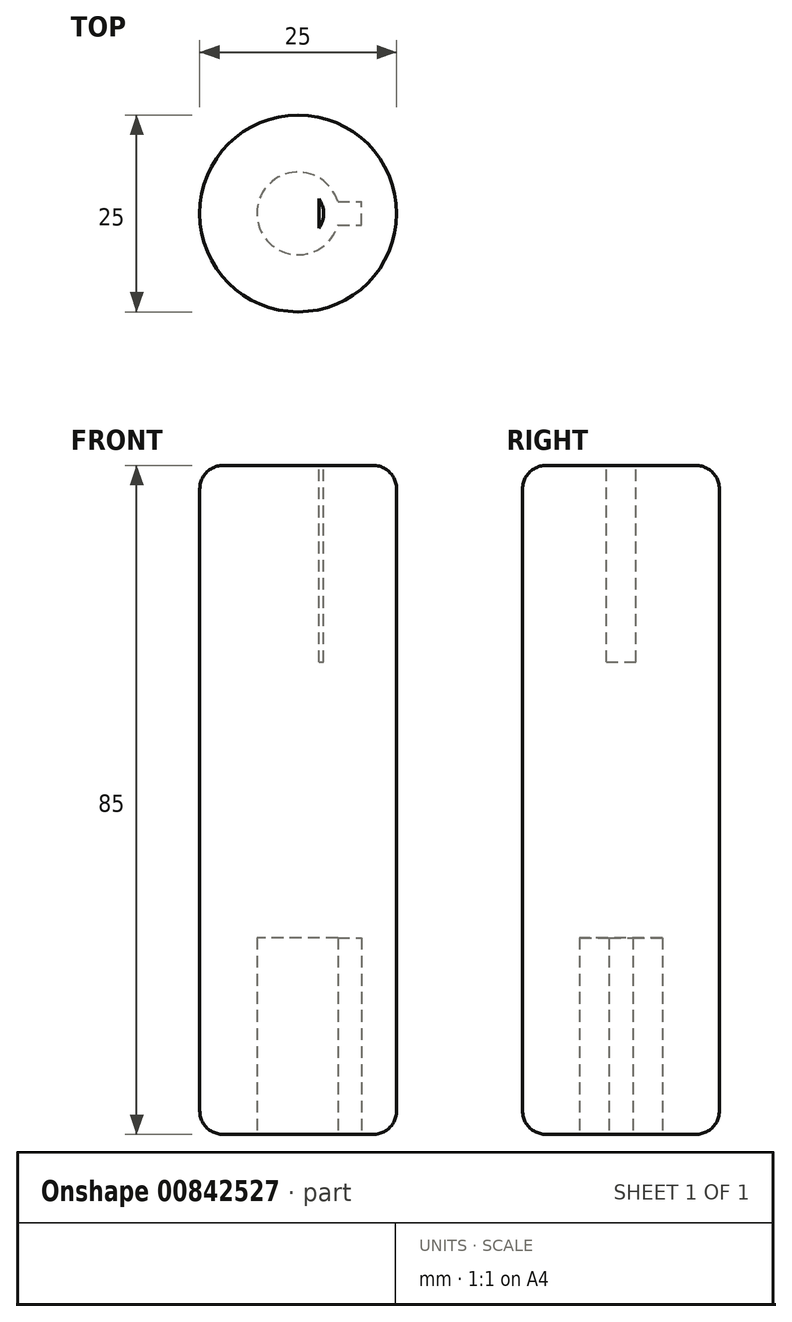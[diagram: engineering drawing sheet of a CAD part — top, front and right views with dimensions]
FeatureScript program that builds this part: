
annotation { "Feature Type Name" : "Feature", "Feature Type Description" : "" }
export const myFeature = defineFeature(function(context is Context, id is Id, definition is map)
    precondition{}
    {
        {
            var Q0;
            Q0=qCreatedBy(makeId("Top.planeOp"),FACE);
            var sketch = newSketch(context, id + "F0", { "sketchPlane" : qUnion([Q0])});
            skCircle(sketch, "E0", {"center": v(0, 0) * mm, "radius": 5.25 * mm});
            skCircle(sketch, "E1", {"center": v(0, 0) * mm, "radius": 12.5 * mm});
            skLineSegment(sketch, "E2.bottom", {"start": v(5.03, -1.5) * mm, "end": v(8.03, -1.5) * mm});
            skLineSegment(sketch, "E2.top", {"start": v(5.03, 1.5) * mm, "end": v(8.03, 1.5) * mm});
            skLineSegment(sketch, "E2.left", {"start": v(5.03, -1.5) * mm, "end": v(5.03, 1.5) * mm});
            skLineSegment(sketch, "E2.right", {"start": v(8.03, -1.5) * mm, "end": v(8.03, 1.5) * mm});
            skSolve(sketch);
        }
        {
            var Q0;
            Q0=makeQuery(id+"F0.imprint","IMPRINT",FACE,{"disambiguationData":[TD([[makeQuery(id+"F0.imprint","IMPRINT",EDGE,{"derivedFrom":sQuery(id+"F0.wireOp",EDGE,"E1")}),1.0]])]});
            var Q1;
            {var subQ0=sQuery(id+"F0.wireOp",EDGE,"E2.left");Q1=makeQuery(id+"F0.imprint","IMPRINT",FACE,{"disambiguationData":[TD([[makeQuery(id+"F0.imprint","IMPRINT",EDGE,{"derivedFrom":subQ0}),1.0]])]});}
            var Q2;
            {var subQ1=sQuery(id+"F0.wireOp",EDGE,"E2.bottom");Q2=makeQuery(id+"F0.imprint","IMPRINT",FACE,{"disambiguationData":[TD([[makeQuery(id+"F0.imprint","IMPRINT",EDGE,{"derivedFrom":subQ1}),1.0]])]});}
            var Q3;
            {var subQ0=sQuery(id+"F0.wireOp",EDGE,"E2.left");Q3=makeQuery(id+"F0.imprint","IMPRINT",FACE,{"disambiguationData":[TD([[makeQuery(id+"F0.imprint","IMPRINT",EDGE,{"derivedFrom":subQ0}),-1.0]])]});}
            extrude(context, id + "F1", {"entities" : qUnion([Q0, Q1, Q2, Q3]), "depth" : 85 * mm, "offsetDistance" : 25 * mm});
        }
        {
            var Q0;
            {var subQ0=sQuery(id+"F0.wireOp",EDGE,"E2.left");Q0=makeQuery(id+"F0.imprint","IMPRINT",FACE,{"disambiguationData":[TD([[makeQuery(id+"F0.imprint","IMPRINT",EDGE,{"derivedFrom":subQ0}),1.0]])]});}
            var Q1;
            {var subQ0=sQuery(id+"F0.wireOp",EDGE,"E2.left");Q1=makeQuery(id+"F0.imprint","IMPRINT",FACE,{"disambiguationData":[TD([[makeQuery(id+"F0.imprint","IMPRINT",EDGE,{"derivedFrom":subQ0}),-1.0]])]});}
            var Q2;
            {var subQ1=sQuery(id+"F0.wireOp",EDGE,"E2.bottom");Q2=makeQuery(id+"F0.imprint","IMPRINT",FACE,{"disambiguationData":[TD([[makeQuery(id+"F0.imprint","IMPRINT",EDGE,{"derivedFrom":subQ1}),1.0]])]});}
            extrude(context, id + "F2", {"entities" : qUnion([Q0, Q1, Q2]), "operationType" : NewBodyOperationType.REMOVE, "depth" : 25 * mm, "offsetDistance" : 25 * mm});
        }
        {
            var Q0;
            Q0=makeQuery(id+"F1.opExtrude","CAP_FACE",FACE,{"disambiguationData":[OSD([sQuery(id+"F0.wireOp",EDGE,"E1")])],"isStart":false});
            var sketch = newSketch(context, id + "F3", { "sketchPlane" : qUnion([Q0])});
            skCircle(sketch, "E3", {"center": v(0, 0) * mm, "radius": 3.23 * mm});
            skLineSegment(sketch, "E4", {"start": v(2.62, -5.56) * mm, "end": v(2.62, 8.18) * mm});
            skPoint(sketch, "E5", {"position": v(2.62, -1.87) * mm});
            skPoint(sketch, "E6", {"position": v(2.62, 1.87) * mm});
            skSolve(sketch);
        }
        {
            var Q0;
            {var subQ0=sQuery(id+"F3.wireOp",EDGE,"E4");var subQ1=sQuery(id+"F3.wireOp",EDGE,"E3");var subQ2=makeQuery(id+"F3.imprint","INTERSECT",VERTEX,{"disambiguationData":[OD(0.0)],"derivedFrom":[subQ1,subQ0]});Q0=makeQuery(id+"F3.imprint","IMPRINT",FACE,{"disambiguationData":[TD([[makeQuery(id+"F3.imprint","IMPRINT",EDGE,{"disambiguationData":[TD([[subQ2,1.0]])],"derivedFrom":subQ1}),1.0]])]});}
            extrude(context, id + "F4", {"entities" : qUnion([Q0]), "operationType" : NewBodyOperationType.REMOVE, "oppositeDirection" : true, "depth" : 25 * mm, "offsetDistance" : 25 * mm});
        }
        {
            var Q0;
            Q0=makeQuery(id+"F1.opExtrude","CAP_EDGE",EDGE,{"disambiguationData":[OSD([sQuery(id+"F0.wireOp",EDGE,"E1")])],"isStart":false});
            var Q1;
            Q1=makeQuery(id+"F1.opExtrude","CAP_EDGE",EDGE,{"disambiguationData":[OSD([sQuery(id+"F0.wireOp",EDGE,"E1")])],"isStart":true});
            fillet(context, id + "F5", {"entities" : qUnion([Q0, Q1]), "radius" : 3 * mm, "tangentPropagation" : true, "allowEdgeOverflow" : false});
        }
    });
